# Revit family: VHS-E_Angle_DN15_RFA
name_source: partatom
category: Pipe Accessories
units: mm (PartAtom-declared; Revit-internal decimal feet)

## family parameters
Always vertical = Yes
Cut with Voids When Loaded = No
OmniClass Number = 23.65.55.14.17
OmniClass Title = Adjusting/Controlling Valves for Liquid Services
Part Type = Valve - Breaks Into
Round Connector Dimension = Use Diameter
Shared = No
Work Plane-Based = No

## types (1)
- VHS-E_Angle_DN15-20_013G4691
    Application = 1-pipe system
    D = 20 mm  [stored 0.0656168 ft]
    DR = 15 mm
    Description = Thermostatic H-piece Valve
    H0 = 41 mm
    H1 = 26 mm  [stored 0.0853018 ft]
    H2 = 3 mm  [stored 0.00984252 ft]
    H3 = 3.3 mm
    H4 = 17 mm
    H5 = 2.6 mm
    H6 = 3.6 mm
    HH = 46 mm  [stored 0.150919 ft]
    IfcExportAs = IfcValveType
    IfcExportType = VHS-E
    Kvs = 1.2 m³/h
    L1 = 3 mm  [stored 0.00984252 ft]
    L1__ve = -3 mm  [stored -0.00984252 ft]
    L2 = 0 mm  [stored 0 ft]
    L2_ve = 0 mm  [stored 0 ft]
    L3 = 3.4 mm
    L4 = 3.7 mm
    L4_ve = -3.7 mm  [stored -0.0121391 ft]
    L5_ve = -5 mm  [stored -0.0164042 ft]
    L6_ve = -1.5 mm  [stored -0.00492126 ft]
    L7_ve = -9.9 mm
    LC1 = 50 mm
    LC2 = 0 mm  [stored 0 ft]
    LL1 = 48.4 mm
    LL2 = 22.2 mm  [stored 0.0728346 ft]
    LL3 = 8.1 mm
    LL4 = -0.4 mm
    LL5 = 12 mm  [stored 0.0393701 ft]
    LM = 25 mm  [stored 0.082021 ft]
    LOD 200 = No
    LOD 350 = Yes
    L_EQ = 25 mm  [stored 0.082021 ft]
    Manufacturer = Danfoss
    Max Differential Pressure = 0.6 bar
    Max Medium Temperature = 120 °C
    Max Operating Pressure = 10 bar
    Model = 013G4691
    Model Type = VHS-E_Angle_DN15-20
    RB1 = 11.7 mm  [stored 0.0383858 ft]
    RB2 = 10.3 mm
    RV1 = 10.5 mm  [stored 0.0344488 ft]
    RV10 = 13.2 mm
    RV2 = 12.5 mm  [stored 0.0410105 ft]
    RV3 = 12.3 mm
    RV4 = 11.4 mm
    RV5 = 8 mm  [stored 0.0262467 ft]
    RV6 = 10 mm  [stored 0.0328084 ft]
    RV7 = 9.5 mm  [stored 0.031168 ft]
    RV8 = 1 mm  [stored 0.00328084 ft]
    RV9 = 15 mm  [stored 0.0492126 ft]
    R_nut = 16.8 mm  [stored 0.0551181 ft]
    TD1 = 33.5 mm  [stored 0.109908 ft]
    TD2 = 26.4 mm
    TH1 = 47.3 mm
    URL = https://store.danfoss.com
    Valve Body Material = Danfoss Nickel Plated Brass
    W1 = 13.5 mm  [stored 0.0442913 ft]
    W2 = 26 mm  [stored 0.0853018 ft]
    W_nut1 = 14.5 mm  [stored 0.0475722 ft]
    W_nut2 = 5.2 mm
    Weight = 0.70 kg

note: [stored X ft] marks values corroborated as IEEE doubles in the binary element streams (Revit-internal decimal feet)

## geometry (parser evidence)
native form markers: Sweep x4
no freeform markers — native parametric forms only
